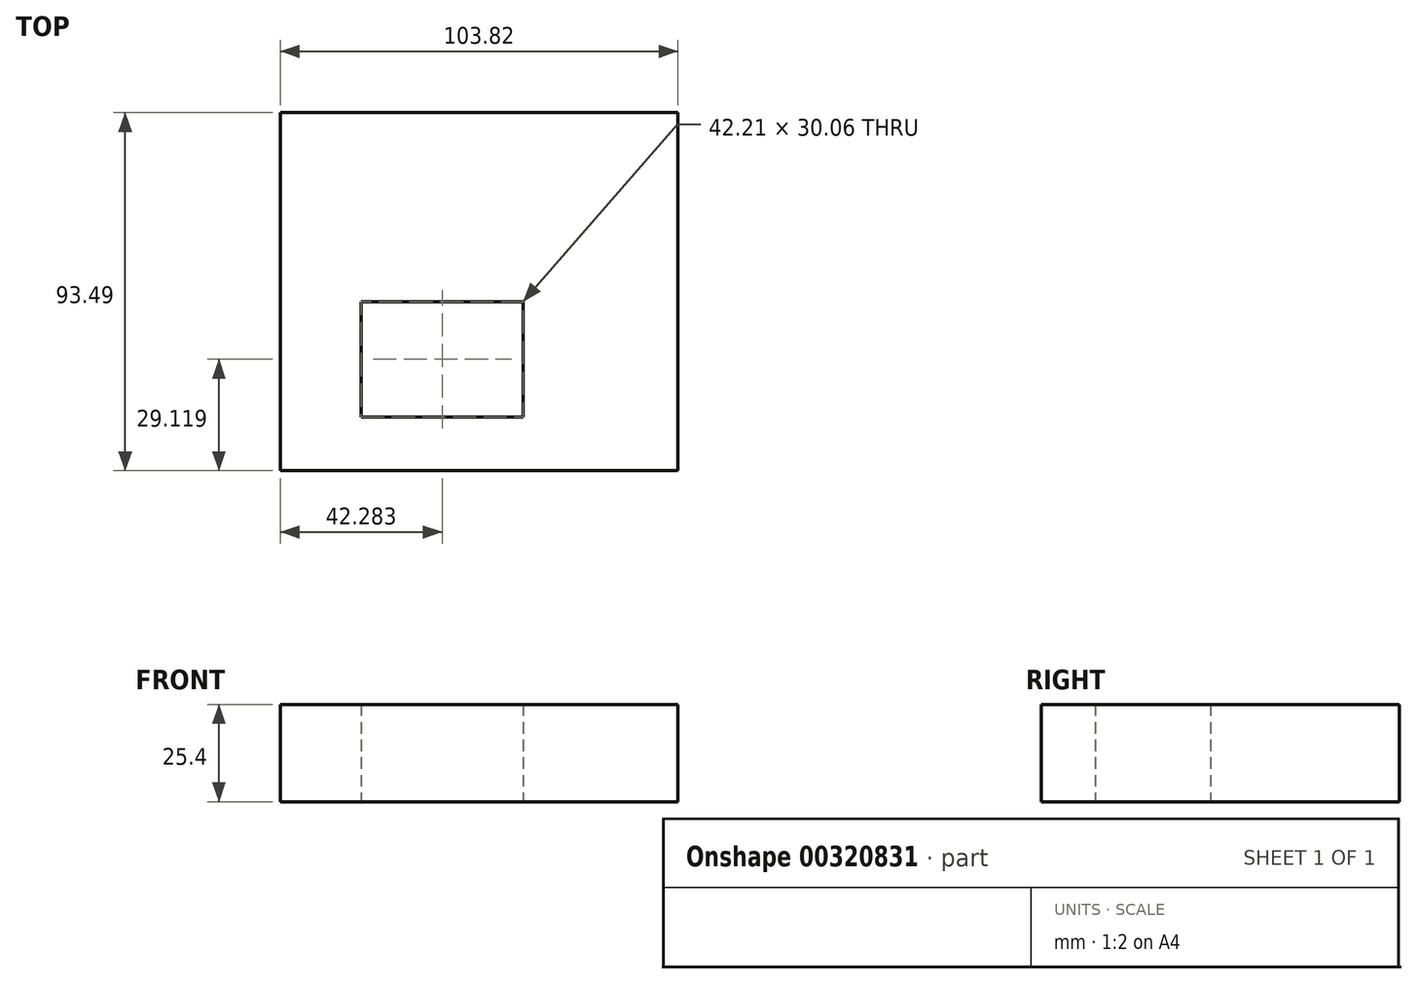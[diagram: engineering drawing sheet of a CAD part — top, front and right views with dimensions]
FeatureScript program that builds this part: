
annotation { "Feature Type Name" : "Feature", "Feature Type Description" : "" }
export const myFeature = defineFeature(function(context is Context, id is Id, definition is map)
    precondition{}
    {
        {
            var Q0;
            Q0=qCreatedBy(makeId("Top.planeOp"),FACE);
            var sketch = newSketch(context, id + "F0", { "sketchPlane" : qUnion([Q0])});
            skLineSegment(sketch, "E0", {"start": v(-43.54, 49.34) * mm, "end": v(-43.54, -44.15) * mm});
            skLineSegment(sketch, "E1", {"start": v(-43.54, -44.15) * mm, "end": v(34.88, -44.15) * mm});
            skLineSegment(sketch, "E2", {"start": v(34.88, -44.15) * mm, "end": v(34.88, 49.34) * mm});
            skLineSegment(sketch, "E3", {"start": v(34.88, 49.34) * mm, "end": v(-43.54, 49.34) * mm});
            skLineSegment(sketch, "E4", {"start": v(-22.36, 0) * mm, "end": v(-22.36, 0) * mm});
            skLineSegment(sketch, "E5", {"start": v(-22.36, 0) * mm, "end": v(-22.36, -30.06) * mm});
            skLineSegment(sketch, "E6", {"start": v(-22.36, -30.06) * mm, "end": v(19.85, -30.06) * mm});
            skLineSegment(sketch, "E7", {"start": v(19.85, 0) * mm, "end": v(-22.36, 0) * mm});
            skLineSegment(sketch, "E8", {"start": v(19.85, 0) * mm, "end": v(19.85, -30.06) * mm});
            skSolve(sketch);
        }
        {
            var Q0;
            Q0=makeQuery(id+"F0.imprint","IMPRINT",FACE,{"disambiguationData":[TD([[makeQuery(id+"F0.imprint","IMPRINT",EDGE,{"derivedFrom":sQuery(id+"F0.wireOp",EDGE,"E0")}),1.0]])]});
            extrude(context, id + "F1", {"entities" : qUnion([Q0]), "depth" : 25.4 * mm});
        }
        {
            var Q0;
            Q0=makeQuery(id+"F1.opExtrude","SWEPT_FACE",FACE,{"disambiguationData":[OSD([sQuery(id+"F0.wireOp",EDGE,"E2")])]});
            var sketch = newSketch(context, id + "F2", { "sketchPlane" : qUnion([Q0])});
            skLineSegment(sketch, "E9", {"start": v(49.34, 12.7) * mm, "end": v(-44.15, 25.4) * mm});
            skLineSegment(sketch, "E10", {"start": v(-44.15, 25.4) * mm, "end": v(49.34, 25.4) * mm});
            skLineSegment(sketch, "E11", {"start": v(49.34, 25.4) * mm, "end": v(49.34, 12.7) * mm});
            skSolve(sketch);
        }
        {
            var Q0;
            {var subQ0=sQuery(id+"F2.wireOp",EDGE,"E9");Q0=makeQuery(id+"F2.imprint","IMPRINT",FACE,{"disambiguationData":[TD([[makeQuery(id+"F2.imprint","IMPRINT",EDGE,{"derivedFrom":subQ0}),1.0]])]});}
            var Q1;
            Q1=makeQuery(id+"F2.imprint","IMPRINT",FACE,{"disambiguationData":[TD([[makeQuery(id+"F2.imprint","IMPRINT",EDGE,{"derivedFrom":sQuery(id+"F2.wireOp",EDGE,"E9")}),-1.0]])]});
            extrude(context, id + "F3", {"entities" : qUnion([Q0, Q1]), "operationType" : NewBodyOperationType.ADD, "depth" : 25.4 * mm});
        }
    });
